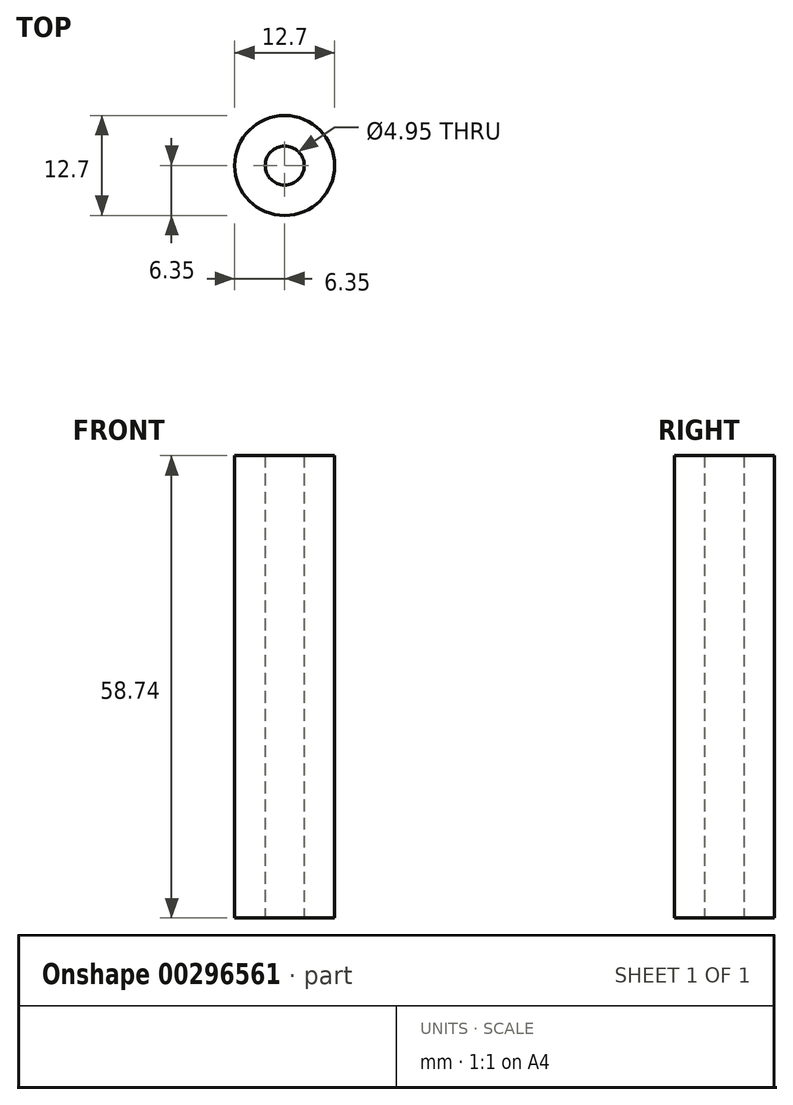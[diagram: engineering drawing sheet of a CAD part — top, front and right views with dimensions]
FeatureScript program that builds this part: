
annotation { "Feature Type Name" : "Feature", "Feature Type Description" : "" }
export const myFeature = defineFeature(function(context is Context, id is Id, definition is map)
    precondition{}
    {
        {
            var Q0;
            Q0=qCreatedBy(makeId("Top.planeOp"),FACE);
            var sketch = newSketch(context, id + "F0", { "sketchPlane" : qUnion([Q0])});
            skCircle(sketch, "E0", {"center": v(0, 0) * mm, "radius": 2.48 * mm});
            skCircle(sketch, "E1", {"center": v(0, 0) * mm, "radius": 6.35 * mm});
            skSolve(sketch);
        }
        {
            var Q0;
            Q0=qSketchRegion(id+"F0",true);
            extrude(context, id + "F1", {"entities" : qUnion([Q0]), "depth" : 58.74 * mm});
        }
    });
